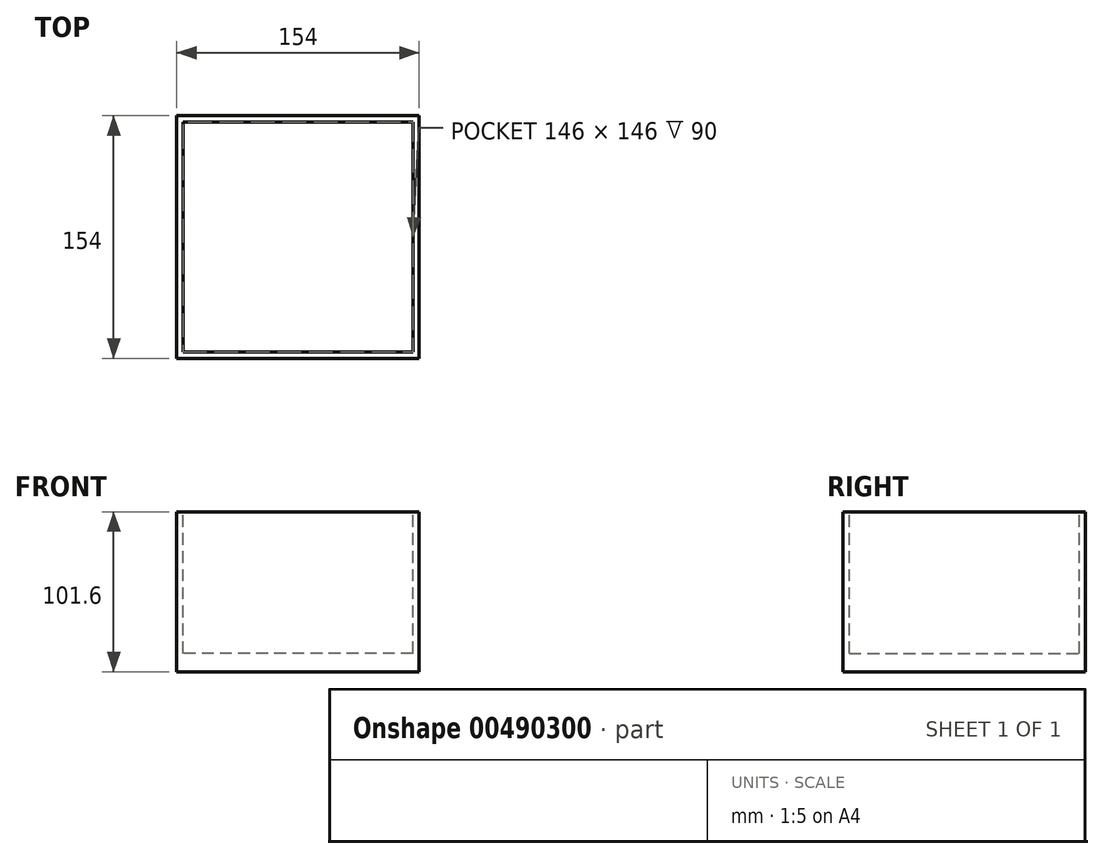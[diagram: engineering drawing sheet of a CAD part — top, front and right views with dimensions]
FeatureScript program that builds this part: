
annotation { "Feature Type Name" : "Feature", "Feature Type Description" : "" }
export const myFeature = defineFeature(function(context is Context, id is Id, definition is map)
    precondition{}
    {
        {
            var Q0;
            Q0=qCreatedBy(makeId("Top.planeOp"),FACE);
            var sketch = newSketch(context, id + "F0", { "sketchPlane" : qUnion([Q0])});
            skLineSegment(sketch, "E0.bottom", {"start": v(77, -77) * mm, "end": v(-77, -77) * mm});
            skLineSegment(sketch, "E0.top", {"start": v(77, 77) * mm, "end": v(-77, 77) * mm});
            skLineSegment(sketch, "E0.left", {"start": v(77, -77) * mm, "end": v(77, 77) * mm});
            skLineSegment(sketch, "E0.right", {"start": v(-77, -77) * mm, "end": v(-77, 77) * mm});
            skPoint(sketch, "E0.middle", {"position": v(0, 0) * mm});
            skSolve(sketch);
        }
        {
            var Q0;
            Q0 = qSketchRegion(id + "F0", true);
            extrude(context, id + "F1", {"entities" : qUnion([Q0]), "depth" : 101.6 * mm, "offsetDistance" : 25 * mm});
        }
        {
            var Q0;
            Q0=makeQuery(id+"F1.opExtrude","CAP_FACE",FACE,{"disambiguationData":[OSD([sQuery(id+"F0.wireOp",EDGE,"E0.bottom"),sQuery(id+"F0.wireOp",EDGE,"E0.top"),sQuery(id+"F0.wireOp",EDGE,"E0.left"),sQuery(id+"F0.wireOp",EDGE,"E0.right")])],"isStart":false});
            var sketch = newSketch(context, id + "F2", { "sketchPlane" : qUnion([Q0])});
            skLineSegment(sketch, "E1.bottom", {"start": v(73, -73) * mm, "end": v(-73, -73) * mm});
            skLineSegment(sketch, "E1.top", {"start": v(73, 73) * mm, "end": v(-73, 73) * mm});
            skLineSegment(sketch, "E1.left", {"start": v(73, -73) * mm, "end": v(73, 73) * mm});
            skLineSegment(sketch, "E1.right", {"start": v(-73, -73) * mm, "end": v(-73, 73) * mm});
            skPoint(sketch, "E1.middle", {"position": v(0, 0) * mm});
            skSolve(sketch);
        }
        {
            var Q0;
            Q0 = qSketchRegion(id + "F2", true);
            extrude(context, id + "F3", {"entities" : qUnion([Q0]), "operationType" : NewBodyOperationType.REMOVE, "oppositeDirection" : true, "depth" : 90 * mm, "offsetDistance" : 25 * mm});
        }
    });
